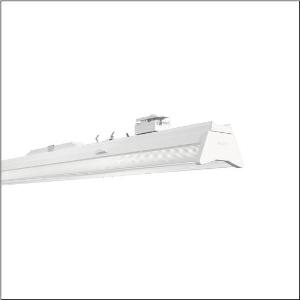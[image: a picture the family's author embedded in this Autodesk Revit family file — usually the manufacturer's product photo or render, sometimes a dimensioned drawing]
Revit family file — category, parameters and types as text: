
# Revit family: licross_r__11_performance_tw_51tm16tnt45x_2116
name_source: partatom
category: Lighting Fixtures
units: mm (PartAtom-declared; Revit-internal decimal feet)

## family parameters
Cut with Voids When Loaded = No
Host = Face
Light Source = No
Part Type = Normal
Room Calculation Point = No
Round Connector Dimension = Use Diameter
Shared = No

## types (1)
- --- (1 x LED 2700 K ... 6500 K, 4700 lm, 28.9 W, 2700K)
    Apparent Load = 29 VA
    CIE Flux Codes = 63 87 95 78 100
    Color Rendering = 80
    Color Temperature = 2700K
    Default Elevation = 1800 mm
    Description = Licross® 11 Performance TW, luminaire insert, of sheet steel, galvanised, coil coated, white, length: 1.500mm, width: 120mm, height: 123mm, LED rated luminous flux: 4.700lm, light colour: 8tw, control gear: DALI DT8, with plug, 5-pole, with phase selection, mains connection: 220..240V, AC, 50/60Hz, rated input power: 28.9W, halogen-free wiring, primary light control with lens, of plastic, primary optical cover: cover, of PMMA, light emission: direct/indirect distribution, primary light characteristic: symmetric, protection rating (complete): IP40, insulation class (complete): insulation class I (protective earthing), certification: CE, ENEC, VDE, UKCA, protection symbol: D if used in an environment without relevant dust loads with corresponding accessories, impact resistance: IK06, permissible ambient temperature for indoor applications: -25..+45°C, corresponds to IFS (International Featured Standards) requirements for safety and quality in the food industry, reducing of maximum allowable ambient temperature of 5°C with ceiling mounting, LABS conformity tested according to VDMA 24364:2018-05, packaging unit: 1 piece
    Height = 114 mm
    Lamp = 1 x LED 2700 K ... 6500 K
    Lamp Light Flux = 4700 lm
    Lamp Power = 28.9 W
    Lamp count = 1
    Length = 1500 mm
    Luminous efficacy = 163 lm/W
    Manufacturer = Siteco
    ModVariant = No
    Model = 51TM16TNT45X
    Mounting Place = Ceiling
    Mounting Type = Pendant
    Number of Poles = 1
    OnlyDefault = Yes
    Power Factor = 1
    Product Name = Licross® 11 Performance TW
    Product group = luminaire insert
    ProductGroupID = 901
    Protection Class = Protection class I
    Protection Degree = IP 40
    RLX_Detail_Level = 1
    RLX_Emergency_Light_Flux = 0 lm
    RLX_Emergency_Type = 0
    RLX_Emergency_Type_DB = No
    RlxData = <blob elided: 30333 chars, md5=82ac79a8>
    Socket = socket
    Standby Power = 0 W
    System Light Flux = 4700 lm
    System Power = 29 W
    Type Comments = individual setting: CCT=2700K
    Type Image = l_1256138.jpg
    URL = http://relux.com
    VarID = @adj_007065
    Voltage = 0 V
    Weight = 0.00 kg
    Width = 120 mm

## geometry (parser evidence)
native form markers: Blend x4, Sweep x14
no freeform markers — native parametric forms only
